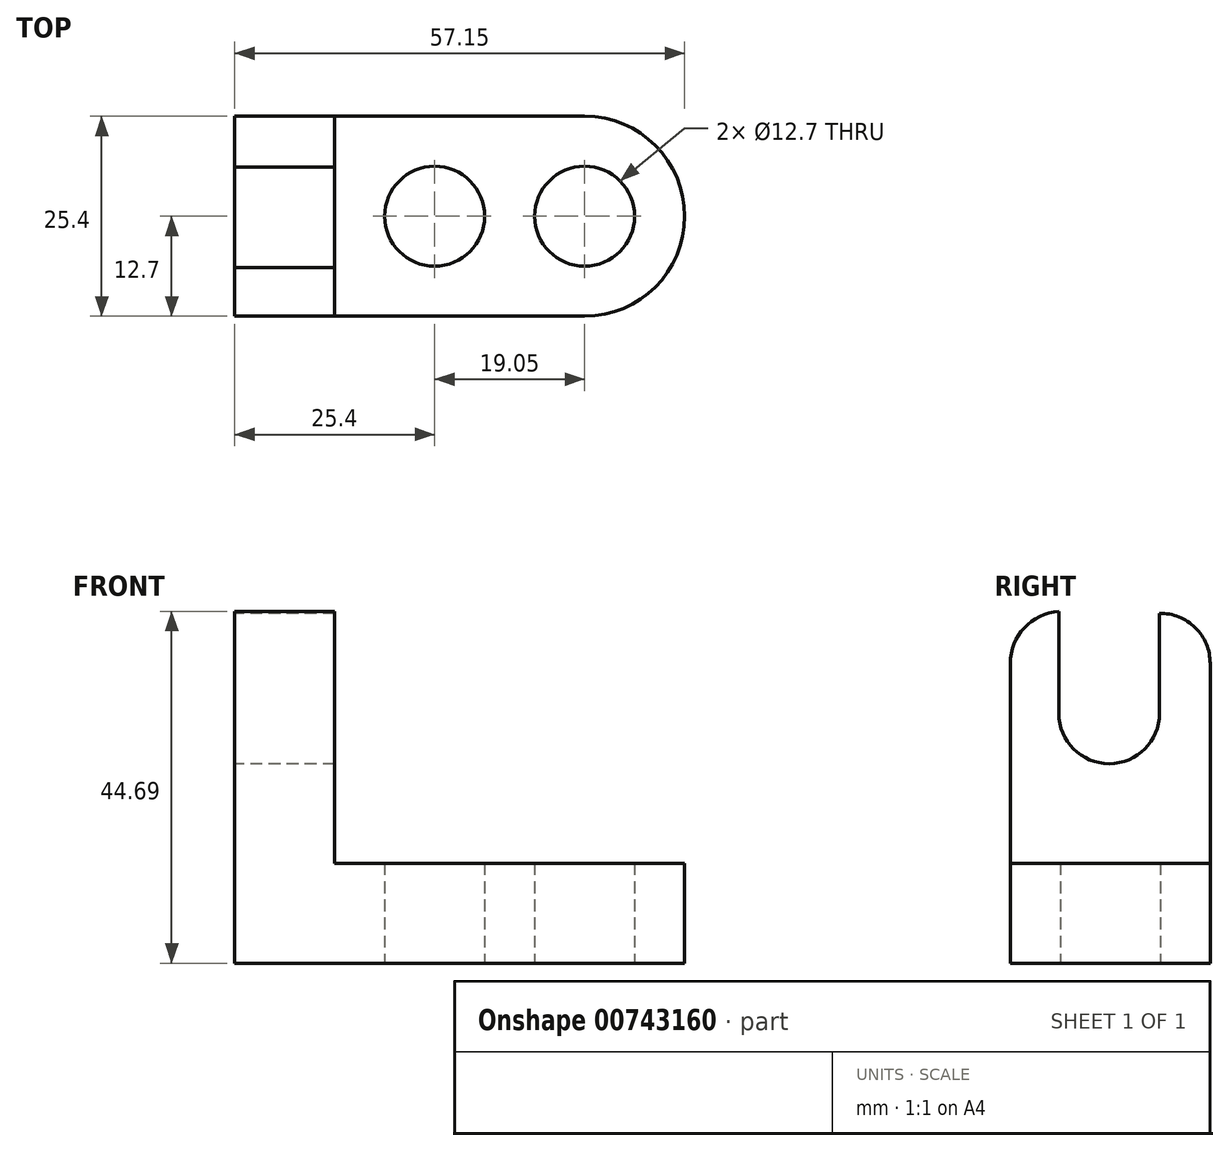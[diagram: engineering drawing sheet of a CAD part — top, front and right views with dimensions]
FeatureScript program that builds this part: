
annotation { "Feature Type Name" : "Feature", "Feature Type Description" : "" }
export const myFeature = defineFeature(function(context is Context, id is Id, definition is map)
    precondition{}
    {
        {
            var Q0;
            Q0=qCreatedBy(makeId("Top.planeOp"),FACE);
            var sketch = newSketch(context, id + "F0", { "sketchPlane" : qUnion([Q0])});
            skLineSegment(sketch, "E0.bottom", {"start": v(0, 0) * mm, "end": v(44.45, 0) * mm});
            skLineSegment(sketch, "E0.top", {"start": v(0, 25.4) * mm, "end": v(44.45, 25.4) * mm});
            skLineSegment(sketch, "E0.left", {"start": v(0, 0) * mm, "end": v(0, 25.4) * mm});
            skLineSegment(sketch, "E0.right", {"start": v(44.45, 0) * mm, "end": v(44.45, 25.4) * mm});
            skArc(sketch, "E1", {"start": v(44.45, 0) * mm, "mid": v(57.15, 12.7) * mm, "end": v(44.45, 25.4) * mm});
            skCircle(sketch, "E2", {"center": v(44.45, 12.7) * mm, "radius": 6.35 * mm});
            skCircle(sketch, "E3", {"center": v(25.4, 12.7) * mm, "radius": 6.35 * mm});
            skSolve(sketch);
        }
        {
            var Q0;
            {var subQ2=sQuery(id+"F0.wireOp",EDGE,"E0.bottom");Q0=makeQuery(id+"F0.imprint","IMPRINT",FACE,{"disambiguationData":[TD([[makeQuery(id+"F0.imprint","IMPRINT",EDGE,{"derivedFrom":subQ2}),1.0]])]});}
            var Q1;
            {var subQ0=sQuery(id+"F0.wireOp",EDGE,"E1");Q1=makeQuery(id+"F0.imprint","IMPRINT",FACE,{"disambiguationData":[TD([[makeQuery(id+"F0.imprint","IMPRINT",EDGE,{"derivedFrom":subQ0}),1.0]])]});}
            extrude(context, id + "F1", {"entities" : qUnion([Q0, Q1]), "depth" : 12.7 * mm, "offsetDistance" : 25.4 * mm});
        }
        {
            var Q0;
            Q0=makeQuery(id+"F1.opExtrude","SWEPT_FACE",FACE,{"disambiguationData":[OSD([sQuery(id+"F0.wireOp",EDGE,"E0.left")])]});
            var sketch = newSketch(context, id + "F2", { "sketchPlane" : qUnion([Q0])});
            skLineSegment(sketch, "E4", {"start": v(-25.4, 12.7) * mm, "end": v(-25.4, 38.1) * mm});
            skLineSegment(sketch, "E5", {"start": v(-25.4, 38.1) * mm, "end": v(-18.98, 38.1) * mm});
            skLineSegment(sketch, "E6", {"start": v(-18.98, 38.1) * mm, "end": v(-18.98, 44.45) * mm});
            skLineSegment(sketch, "E7", {"start": v(-18.98, 44.45) * mm, "end": v(-18.98, 31.75) * mm});
            skLineSegment(sketch, "E8", {"start": v(-18.98, 31.75) * mm, "end": v(-6.17, 31.75) * mm});
            skLineSegment(sketch, "E9", {"start": v(-6.17, 31.75) * mm, "end": v(-6.17, 44.69) * mm});
            skLineSegment(sketch, "E10", {"start": v(-6.17, 44.69) * mm, "end": v(-6.4, 38.34) * mm});
            skLineSegment(sketch, "E11", {"start": v(-6.4, 38.34) * mm, "end": v(0, 38.1) * mm});
            skLineSegment(sketch, "E12", {"start": v(0, 38.1) * mm, "end": v(0, 12.7) * mm});
            skLineSegment(sketch, "E13", {"start": v(0, 12.7) * mm, "end": v(-25.4, 12.7) * mm});
            skArc(sketch, "E14", {"start": v(0, 38.1) * mm, "mid": v(-1.78, 42.61) * mm, "end": v(-6.17, 44.69) * mm});
            skArc(sketch, "E15", {"start": v(-18.98, 44.45) * mm, "mid": v(-23.51, 42.62) * mm, "end": v(-25.4, 38.1) * mm});
            skArc(sketch, "E16", {"start": v(-18.98, 31.75) * mm, "mid": v(-12.57, 25.35) * mm, "end": v(-6.17, 31.75) * mm});
            skSolve(sketch);
        }
        {
            var Q0;
            Q0=makeQuery(id+"F2.imprint","IMPRINT",FACE,{"disambiguationData":[TD([[makeQuery(id+"F2.imprint","IMPRINT",EDGE,{"derivedFrom":sQuery(id+"F2.wireOp",EDGE,"E4")}),-1.0]])]});
            var Q1;
            {var subQ0=sQuery(id+"F2.wireOp",EDGE,"E14");Q1=makeQuery(id+"F2.imprint","IMPRINT",FACE,{"disambiguationData":[TD([[makeQuery(id+"F2.imprint","IMPRINT",EDGE,{"derivedFrom":subQ0}),1.0]])]});}
            var Q2;
            {var subQ0=sQuery(id+"F2.wireOp",EDGE,"E5");Q2=makeQuery(id+"F2.imprint","IMPRINT",FACE,{"disambiguationData":[TD([[makeQuery(id+"F2.imprint","IMPRINT",EDGE,{"derivedFrom":subQ0}),1.0]])]});}
            extrude(context, id + "F3", {"entities" : qUnion([Q0, Q1, Q2]), "operationType" : NewBodyOperationType.ADD, "oppositeDirection" : true, "depth" : 12.7 * mm, "offsetDistance" : 25.4 * mm});
        }
    });
